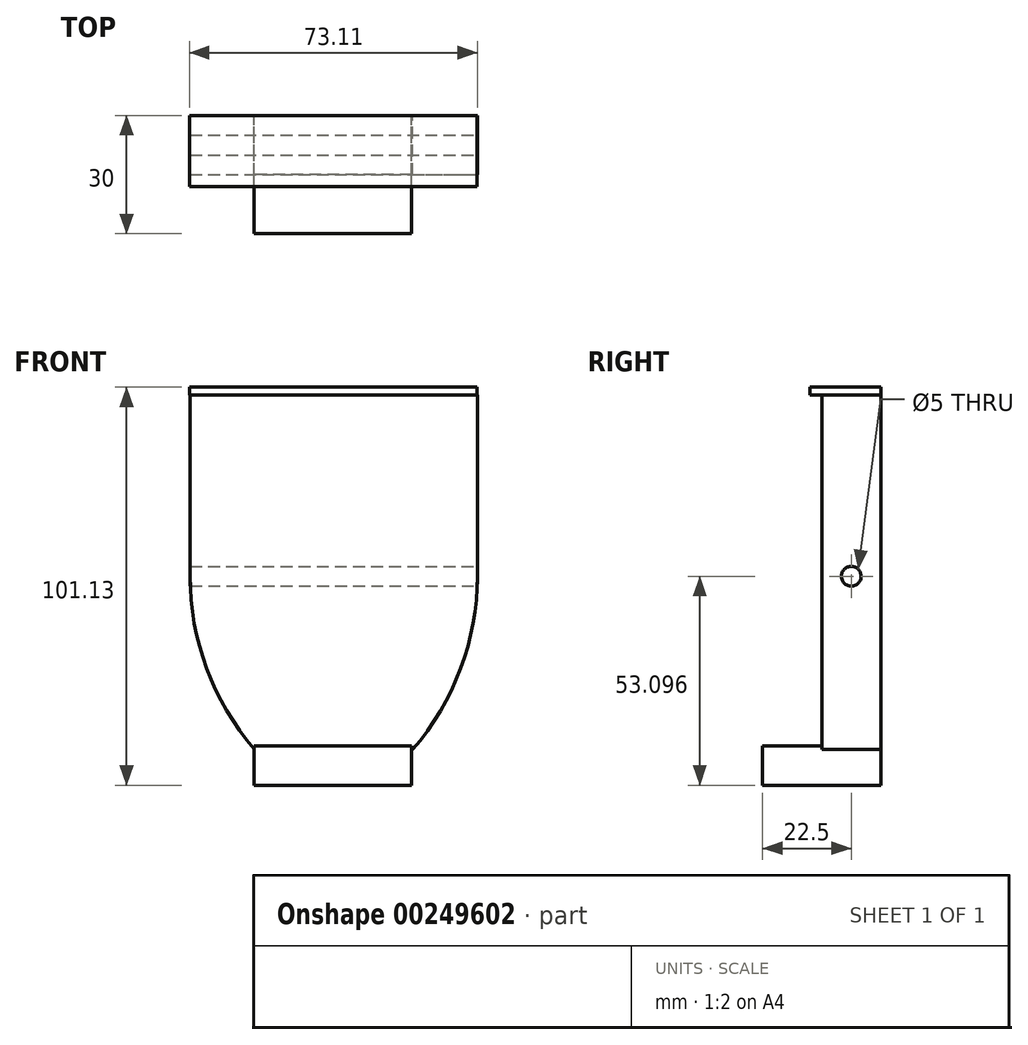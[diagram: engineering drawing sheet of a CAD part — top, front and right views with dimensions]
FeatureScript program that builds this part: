
annotation { "Feature Type Name" : "Feature", "Feature Type Description" : "" }
export const myFeature = defineFeature(function(context is Context, id is Id, definition is map)
    precondition{}
    {
        {
            assignVariable(context, id + "F0", {"name" : "thickness", "anyValue" : 15});
        }
        {
            var Q0;
            Q0=qCreatedBy(makeId("Front.planeOp"),FACE);
            var sketch = newSketch(context, id + "F1", { "sketchPlane" : qUnion([Q0])});
            skLineSegment(sketch, "E0.top", {"start": v(-26.97, -34.93) * mm, "end": v(13.18, -34.93) * mm});
            skLineSegment(sketch, "E0.left", {"start": v(-43.4, 53.07) * mm, "end": v(-43.4, 2.95) * mm});
            skLineSegment(sketch, "E0.right", {"start": v(29.6, 53.07) * mm, "end": v(29.6, 2.95) * mm});
            skArc(sketch, "E1", {"start": v(-43.4, 9.07) * mm, "mid": v(-43.45, 6) * mm, "end": v(-43.4, 2.95) * mm});
            skArc(sketch, "E2.MirrorCS", {"start": v(29.6, 9.07) * mm, "mid": v(29.66, 6) * mm, "end": v(29.6, 2.95) * mm});
            skPoint(sketch, "E3.orphan", {"position": v(-6.9, 53.07) * mm});
            skPoint(sketch, "E4.end.orphan", {"position": v(29.6, 9.07) * mm});
            skPoint(sketch, "E5.end.orphan", {"position": v(-6.9, -34.93) * mm});
            skPoint(sketch, "E6.orphan", {"position": v(-43.4, -34.93) * mm});
            skPoint(sketch, "E7.orphan", {"position": v(29.6, -34.93) * mm});
            skArc(sketch, "E8", {"start": v(-43.4, 9.07) * mm, "mid": v(-39.13, -14.4) * mm, "end": v(-26.97, -34.93) * mm});
            skArc(sketch, "E9.MirrorCS", {"start": v(29.6, 9.07) * mm, "mid": v(25.35, -14.4) * mm, "end": v(13.18, -34.93) * mm});
            skLineSegment(sketch, "E10", {"start": v(-43.4, 53.07) * mm, "end": v(-43.4, 55.07) * mm});
            skLineSegment(sketch, "E11", {"start": v(-43.4, 55.07) * mm, "end": v(29.6, 55.07) * mm});
            skLineSegment(sketch, "E12", {"start": v(29.6, 53.07) * mm, "end": v(29.6, 55.07) * mm});
            skSolve(sketch);
        }
        {
            var Q0;
            Q0=qCreatedBy(makeId("Front.planeOp"),FACE);
            var sketch = newSketch(context, id + "F2", { "sketchPlane" : qUnion([Q0])});
            skLineSegment(sketch, "E13.bottom", {"start": v(-27.08, -34.03) * mm, "end": v(12.92, -34.03) * mm});
            skLineSegment(sketch, "E13.top", {"start": v(-27.08, -44.03) * mm, "end": v(12.92, -44.03) * mm});
            skLineSegment(sketch, "E13.left", {"start": v(-27.08, -34.03) * mm, "end": v(-27.08, -44.03) * mm});
            skLineSegment(sketch, "E13.right", {"start": v(12.92, -34.03) * mm, "end": v(12.92, -44.03) * mm});
            skSolve(sketch);
        }
        {
            var Q0;
            Q0=qCreatedBy(makeId("Front.planeOp"),FACE);
            var sketch = newSketch(context, id + "F3", { "sketchPlane" : qUnion([Q0])});
            skLineSegment(sketch, "E14", {"start": v(-43.5, 55.1) * mm, "end": v(-43.5, 57.1) * mm});
            skLineSegment(sketch, "E15", {"start": v(-43.5, 57.1) * mm, "end": v(29.5, 57.1) * mm});
            skLineSegment(sketch, "E16", {"start": v(29.5, 57.1) * mm, "end": v(29.5, 55.1) * mm});
            skLineSegment(sketch, "E17", {"start": v(29.5, 55.1) * mm, "end": v(-43.5, 55.1) * mm});
            skSolve(sketch);
        }
        {
            var Q0;
            Q0=makeQuery(id+"F1.imprint","IMPRINT",FACE,{"disambiguationData":[TD([[makeQuery(id+"F1.imprint","IMPRINT",EDGE,{"derivedFrom":sQuery(id+"F1.wireOp",EDGE,"E0.top")}),1.0]])]});
            extrude(context, id + "F4", {"entities" : qUnion([Q0]), "depth" : (getVariable(context, 'thickness')) * mm});
        }
        {
            var Q0;
            Q0=makeQuery(id+"F2.imprint","IMPRINT",FACE,{"disambiguationData":[TD([[makeQuery(id+"F2.imprint","IMPRINT",EDGE,{"derivedFrom":sQuery(id+"F2.wireOp",EDGE,"E13.bottom")}),-1.0]])]});
            extrude(context, id + "F5", {"entities" : qUnion([Q0]), "operationType" : NewBodyOperationType.ADD, "depth" : (15 + getVariable(context, 'thickness')) * mm});
        }
        {
            var Q0;
            Q0=makeQuery(id+"F3.imprint","IMPRINT",FACE,{"disambiguationData":[TD([[makeQuery(id+"F3.imprint","IMPRINT",EDGE,{"derivedFrom":sQuery(id+"F3.wireOp",EDGE,"E14")}),-1.0]])]});
            extrude(context, id + "F6", {"entities" : qUnion([Q0]), "depth" : (3 + getVariable(context, 'thickness')) * mm});
        }
        {
            var Q0;
            Q0=makeQuery(id+"F4.opExtrude","SWEPT_FACE",FACE,{"disambiguationData":[OSD([sQuery(id+"F1.wireOp",EDGE,"E0.right"),sQuery(id+"F1.wireOp",EDGE,"E12")])]});
            var sketch = newSketch(context, id + "F7", { "sketchPlane" : qUnion([Q0])});
            skCircle(sketch, "E18", {"center": v(-7.5, 9.07) * mm, "radius": 2.5 * mm});
            skSolve(sketch);
        }
        {
            var Q0;
            {var subQ0=sQuery(id+"F7.wireOp",EDGE,"E18");var subQ1=makeQuery(id+"F4.opExtrude","SWEPT_EDGE",EDGE,{"disambiguationData":[OSD([sQuery(id+"F1.wireOp",EDGE,"E0.right"),sQuery(id+"F1.wireOp",EDGE,"E2.MirrorCS"),sQuery(id+"F1.wireOp",EDGE,"E9.MirrorCS")])]});var subQ2=makeQuery(id+"F7.imprint","INTERSECT",VERTEX,{"disambiguationData":[OD(0.0)],"derivedFrom":[subQ1,subQ0]});Q0=makeQuery(id+"F7.imprint","IMPRINT",FACE,{"disambiguationData":[TD([[makeQuery(id+"F7.imprint","IMPRINT",EDGE,{"disambiguationData":[TD([[subQ2,1.0]])],"derivedFrom":subQ0}),1.0]])]});}
            var Q1;
            {var subQ0=sQuery(id+"F7.wireOp",EDGE,"E18");var subQ1=makeQuery(id+"F4.opExtrude","SWEPT_EDGE",EDGE,{"disambiguationData":[OSD([sQuery(id+"F1.wireOp",EDGE,"E0.right"),sQuery(id+"F1.wireOp",EDGE,"E2.MirrorCS"),sQuery(id+"F1.wireOp",EDGE,"E9.MirrorCS")])]});var subQ2=makeQuery(id+"F7.imprint","INTERSECT",VERTEX,{"disambiguationData":[OD(0.0)],"derivedFrom":[subQ1,subQ0]});Q1=makeQuery(id+"F7.imprint","IMPRINT",FACE,{"disambiguationData":[TD([[makeQuery(id+"F7.imprint","IMPRINT",EDGE,{"disambiguationData":[TD([[subQ2,-1.0]])],"derivedFrom":subQ0}),1.0]])]});}
            extrude(context, id + "F8", {"entities" : qUnion([Q0, Q1]), "operationType" : NewBodyOperationType.REMOVE, "oppositeDirection" : true, "depth" : 88 * mm});
        }
    });
